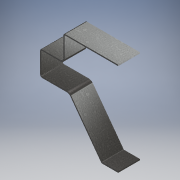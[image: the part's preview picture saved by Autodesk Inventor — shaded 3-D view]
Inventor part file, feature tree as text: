
AUTODESK INVENTOR PART (.ipt)
format: ipt  version: 2017 (Build 210142000, 142)  size: 337,408 bytes
history: native  units: mm
features: extrude x5, sketch x5, fillet x4, other x1
ambient origin geometry x8: Origin, YZ Plane, XZ Plane, XY Plane, X Axis, Y Axis, Z Axis, Center Point
bodies: Body1 (feature_tree)
feature tree (15):
  other  "Sólido1"
  extrude  "Extrusión1"  Depth=101.6mm
  fillet  "Empalme1"  Radius=95.25mm
  fillet  "Empalme2"  Radius=111.125mm
  extrude  "Extrusión2"  Depth=5.0mm TaperAngle=0.0deg
  fillet  "Empalme3"  Radius=12.7mm
  extrude  "Extrusión3"  Depth=76.2mm
  fillet  "Empalme4"  Radius=17.4625mm
  extrude  "Extrusión4"  Depth=76.2mm
  extrude  "Extrusión5"  Depth=88.9mm
  sketch  "Boceto1"  dims[d0=273.05mm d1=101.6mm d2=95.25mm d3=111.125mm]
  sketch  "Boceto2"  dims[d4=393.7mm d7=5.0mm d8=0.0mm d9=12.7mm]
  sketch  "Boceto3"  dims[d10=6.35mm d11=76.2mm d17=17.4625mm]
  sketch  "Boceto4"  dims[d18=19.05mm d19=76.2mm]
  sketch  "Boceto5"  dims[d20=5.55625mm d22=6.35mm d24=38.1mm d27=8.73125mm d38=76.2mm d39=76.2mm d40=158.75mm d42=10.0mm d43=28.575mm d44=42.664062mm d45=8.929688mm d46=0.0mm d47=10.0mm d50=114.3mm d51=133.35mm d52=38.1mm d53=5.55625mm d54=6.35mm d55=47.625mm d56=8.73125mm d57=98.028125mm d58=38.1mm d59=53.975mm d60=53.975mm d61=184.15mm d62=184.15mm d63=38.1mm d64=8.73125mm d65=8.73125mm d66=98.028125mm d67=42.664062mm d68=28.575mm d69=4.7625mm d70=4.7625mm d71=4.7625mm d72=13.096875mm d73=13.096875mm d74=13.096875mm d75=38.1mm d80=63.5mm d81=63.5mm d82=127.0mm d83=3.571875mm d86=12.7mm d87=22.225mm d88=22.225mm d89=25.4mm d90=0.0mm d91=4.7625mm d92=5.0mm d95=5.0mm d96=5.0mm d99=5.0mm d100=5.0mm d101=5.0mm d102=0.0mm d105=0.0mm d109=0.0mm d110=5.0mm d115=17.78mm d117=5.0mm d118=7.73122mm d119=88.9mm d120=0.0mm d121=13.599998mm d122=0.0mm]
